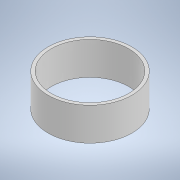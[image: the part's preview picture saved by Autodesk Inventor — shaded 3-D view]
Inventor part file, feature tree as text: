
AUTODESK INVENTOR PART (.ipt)
format: ipt  version: 2020 (Build 240168000, 168)  size: 98,816 bytes
history: native  units: in
note: dims shown in document units (in); Inventor stores cm internally (conversion verified against a paired STEP export)
features: extrude x1, sketch x1
ambient origin geometry x8: Origin, YZ Plane, XZ Plane, XY Plane, X Axis, Y Axis, Z Axis, Center Point
bodies: Solid1 (feature_tree)
feature tree (2):
  extrude  "Extrusion1"  Depth=1.2933in
  sketch  "Sketch1"  dims[d0=3.0512in d1=3.3012in d2=1.2933in d3=0.0in]
